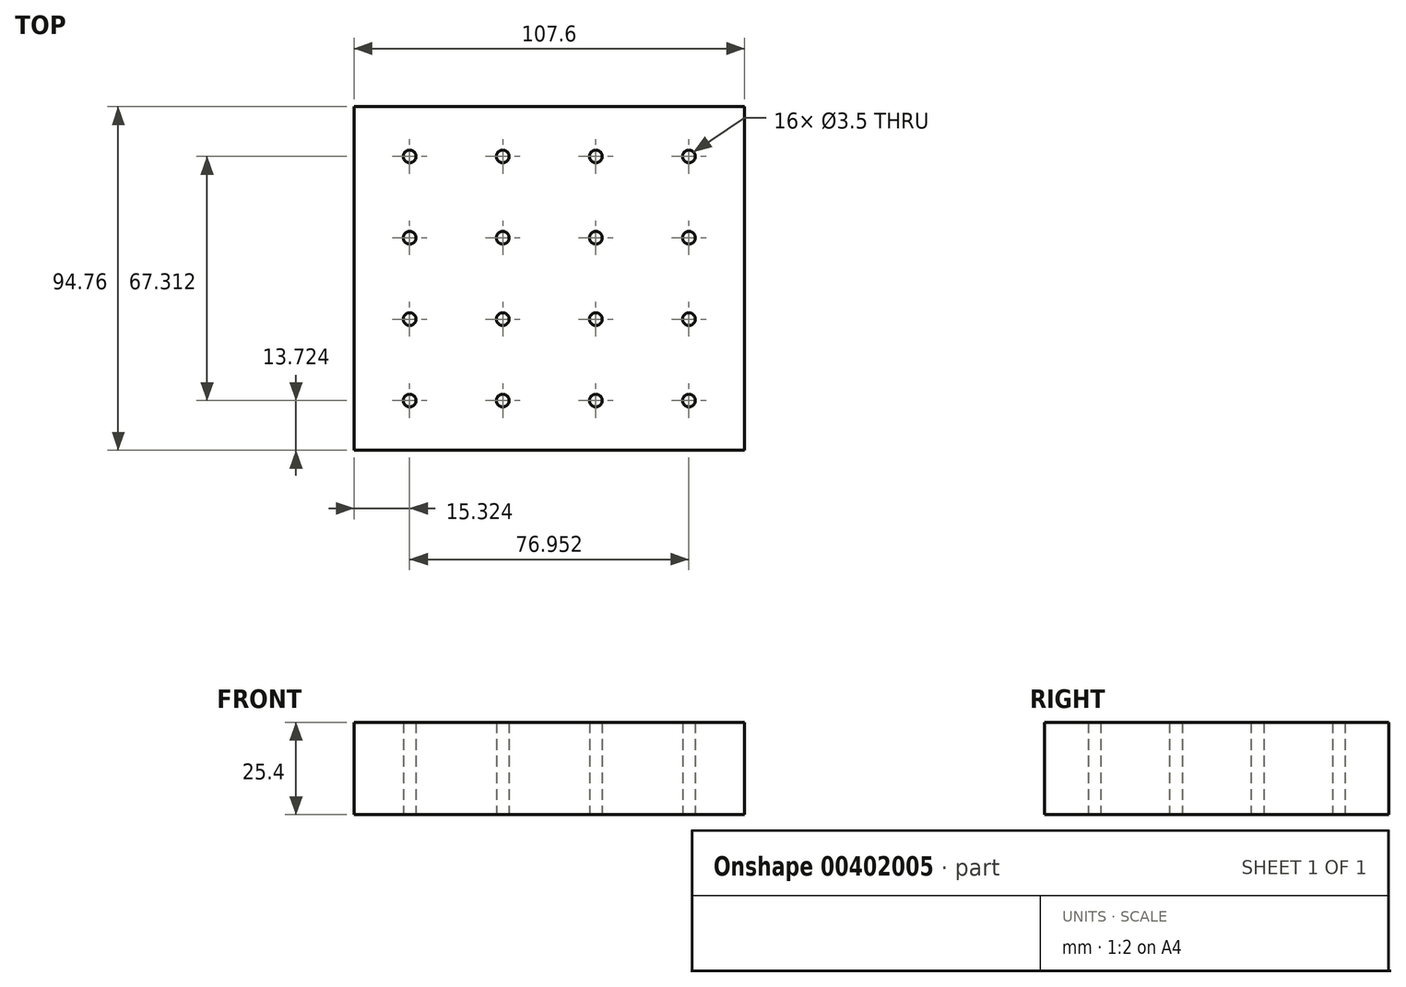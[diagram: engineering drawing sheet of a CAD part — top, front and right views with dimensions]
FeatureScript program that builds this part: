
annotation { "Feature Type Name" : "Feature", "Feature Type Description" : "" }
export const myFeature = defineFeature(function(context is Context, id is Id, definition is map)
    precondition{}
    {
        {
            var Q0;
            Q0=qCreatedBy(makeId("Top.planeOp"),FACE);
            var sketch = newSketch(context, id + "F0", { "sketchPlane" : qUnion([Q0])});
            skLineSegment(sketch, "E0.bottom", {"start": v(-53.8, 47.38) * mm, "end": v(53.8, 47.38) * mm});
            skLineSegment(sketch, "E0.top", {"start": v(-53.8, -47.38) * mm, "end": v(53.8, -47.38) * mm});
            skLineSegment(sketch, "E0.left", {"start": v(-53.8, 47.38) * mm, "end": v(-53.8, -47.38) * mm});
            skLineSegment(sketch, "E0.right", {"start": v(53.8, 47.38) * mm, "end": v(53.8, -47.38) * mm});
            skPoint(sketch, "E0.middle", {"position": v(0, 0) * mm});
            skLineSegment(sketch, "E1", {"start": v(-48.8, 22.44) * mm, "end": v(70.86, 22.44) * mm, "construction": true});
            skPoint(sketch, "E1.endSnap0", {"position": v(48.8, 22.44) * mm});
            skLineSegment(sketch, "E2", {"start": v(-70.29, 0) * mm, "end": v(94.97, 0) * mm, "construction": true});
            skLineSegment(sketch, "E3", {"start": v(-71.7, -22.44) * mm, "end": v(83.03, -22.44) * mm, "construction": true});
            skPoint(sketch, "E3.startSnap0", {"position": v(-48.8, -22.44) * mm});
            skLineSegment(sketch, "E4", {"start": v(-48.8, 22.44) * mm, "end": v(-72.8, 22.44) * mm, "construction": true});
            skLineSegment(sketch, "E5", {"start": v(-70.19, 44.88) * mm, "end": v(60, 44.88) * mm, "construction": true});
            skLineSegment(sketch, "E6", {"start": v(-72.63, -44.88) * mm, "end": v(80.9, -44.88) * mm, "construction": true});
            skLineSegment(sketch, "E7", {"start": v(-51.3, 64.17) * mm, "end": v(-51.3, -68.59) * mm, "construction": true});
            skLineSegment(sketch, "E8", {"start": v(51.3, 61.99) * mm, "end": v(51.3, -75.86) * mm, "construction": true});
            skLineSegment(sketch, "E9", {"start": v(0, 65.14) * mm, "end": v(0, -73.43) * mm, "construction": true});
            skPoint(sketch, "E9.endSnap0", {"position": v(0, -47.38) * mm});
            skLineSegment(sketch, "E10", {"start": v(-25.65, 66.21) * mm, "end": v(-25.65, -75.76) * mm, "construction": true});
            skPoint(sketch, "E10.startSnap0", {"position": v(-25.65, 51.37) * mm});
            skLineSegment(sketch, "E11.MirrorCS", {"start": v(25.65, 66.21) * mm, "end": v(25.65, -75.76) * mm, "construction": true});
            skLineSegment(sketch, "E12", {"start": v(-38.48, 75.36) * mm, "end": v(-38.48, -70.48) * mm, "construction": true});
            skPoint(sketch, "E12.startSnap0", {"position": v(-38.48, 53.13) * mm});
            skLineSegment(sketch, "E13.MirrorCS", {"start": v(-12.83, 75.36) * mm, "end": v(-12.83, -70.48) * mm, "construction": true});
            skLineSegment(sketch, "E14.MirrorCS", {"start": v(12.83, 75.36) * mm, "end": v(12.83, -70.48) * mm, "construction": true});
            skLineSegment(sketch, "E15.MirrorCS", {"start": v(38.48, 75.36) * mm, "end": v(38.48, -70.48) * mm, "construction": true});
            skLineSegment(sketch, "E16", {"start": v(-65.16, 44.88) * mm, "end": v(-65.16, 22.44) * mm, "construction": true});
            skPoint(sketch, "E17.startSnap0", {"position": v(-65.16, 33.66) * mm});
            skLineSegment(sketch, "E18", {"start": v(-92.3, 33.66) * mm, "end": v(103.45, 33.66) * mm, "construction": true});
            skLineSegment(sketch, "E19.MirrorCS", {"start": v(-92.3, 11.22) * mm, "end": v(103.45, 11.22) * mm, "construction": true});
            skLineSegment(sketch, "E20.MirrorCS", {"start": v(-92.3, -11.22) * mm, "end": v(103.45, -11.22) * mm, "construction": true});
            skLineSegment(sketch, "E21.MirrorCS", {"start": v(-92.3, -33.66) * mm, "end": v(103.45, -33.66) * mm, "construction": true});
            skCircle(sketch, "E22", {"center": v(-38.48, 33.66) * mm, "radius": 1.75 * mm});
            skCircle(sketch, "E23.MirrorC", {"center": v(-12.83, 33.66) * mm, "radius": 1.75 * mm});
            skCircle(sketch, "E24.MirrorC", {"center": v(12.83, 33.66) * mm, "radius": 1.75 * mm});
            skCircle(sketch, "E25.MirrorC", {"center": v(38.48, 33.66) * mm, "radius": 1.75 * mm});
            skCircle(sketch, "E26.MirrorC", {"center": v(12.83, 11.22) * mm, "radius": 1.75 * mm});
            skCircle(sketch, "E27.MirrorC", {"center": v(-12.83, 11.22) * mm, "radius": 1.75 * mm});
            skCircle(sketch, "E28.MirrorC", {"center": v(-38.48, 11.22) * mm, "radius": 1.75 * mm});
            skCircle(sketch, "E29.MirrorC", {"center": v(38.48, 11.22) * mm, "radius": 1.75 * mm});
            skCircle(sketch, "E30.MirrorC", {"center": v(-12.83, -11.22) * mm, "radius": 1.75 * mm});
            skCircle(sketch, "E31.MirrorC", {"center": v(-38.48, -11.22) * mm, "radius": 1.75 * mm});
            skCircle(sketch, "E32.MirrorC", {"center": v(-38.48, -33.66) * mm, "radius": 1.75 * mm});
            skCircle(sketch, "E33.MirrorC", {"center": v(12.83, -33.66) * mm, "radius": 1.75 * mm});
            skCircle(sketch, "E34.MirrorC", {"center": v(-12.83, -33.66) * mm, "radius": 1.75 * mm});
            skCircle(sketch, "E35.MirrorC", {"center": v(38.48, -33.66) * mm, "radius": 1.75 * mm});
            skCircle(sketch, "E36.MirrorC", {"center": v(38.48, -11.22) * mm, "radius": 1.75 * mm});
            skCircle(sketch, "E37.MirrorC", {"center": v(12.83, -11.22) * mm, "radius": 1.75 * mm});
            skSolve(sketch);
        }
        {
            var Q0;
            Q0 = qSketchRegion(id + "F0", true);
            extrude(context, id + "F1", {"entities" : qUnion([Q0]), "depth" : 25.4 * mm});
        }
    });
